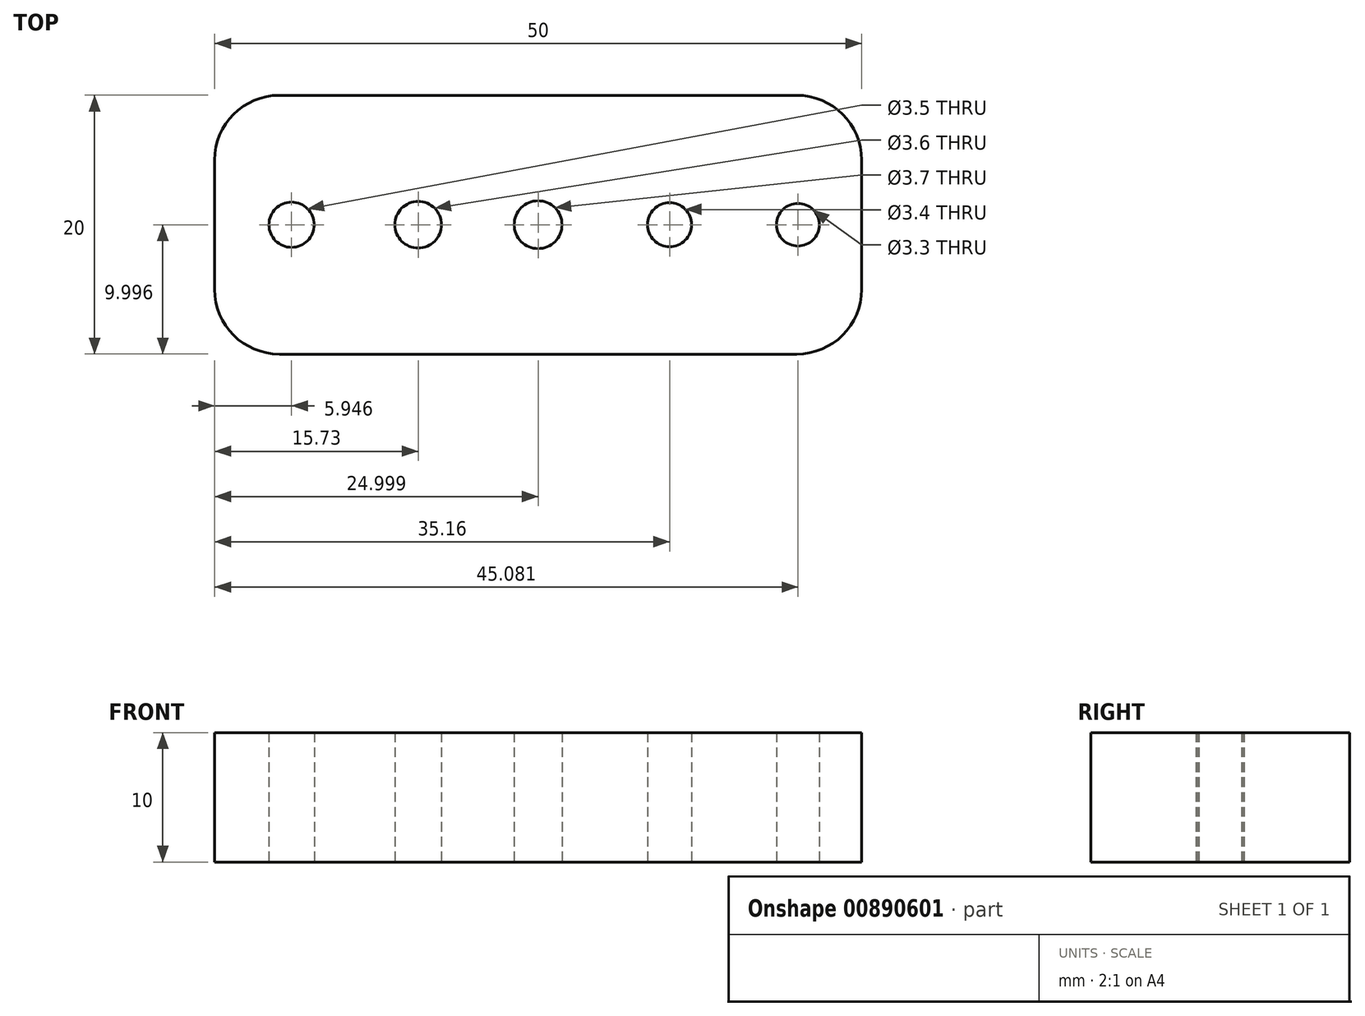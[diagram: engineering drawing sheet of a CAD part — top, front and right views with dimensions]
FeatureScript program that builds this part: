
annotation { "Feature Type Name" : "Feature", "Feature Type Description" : "" }
export const myFeature = defineFeature(function(context is Context, id is Id, definition is map)
    precondition{}
    {
        {
            var Q0;
            Q0=qCreatedBy(makeId("Top.planeOp"),FACE);
            var sketch = newSketch(context, id + "F0", { "sketchPlane" : qUnion([Q0])});
            skLineSegment(sketch, "E0.bottom", {"start": v(-35.16, 0.49) * mm, "end": v(14.84, 0.49) * mm});
            skLineSegment(sketch, "E0.top", {"start": v(-35.16, -19.51) * mm, "end": v(14.84, -19.51) * mm});
            skLineSegment(sketch, "E0.left", {"start": v(-35.16, 0.49) * mm, "end": v(-35.16, -19.51) * mm});
            skLineSegment(sketch, "E0.right", {"start": v(14.84, 0.49) * mm, "end": v(14.84, -19.51) * mm});
            skLineSegment(sketch, "E1", {"start": v(-35.16, -9.51) * mm, "end": v(14.84, -9.51) * mm, "construction": true});
            skCircle(sketch, "E2", {"center": v(-29.21, -9.51) * mm, "radius": 1.75 * mm});
            skCircle(sketch, "E3", {"center": v(-19.43, -9.51) * mm, "radius": 1.8 * mm});
            skCircle(sketch, "E4", {"center": v(-10.16, -9.51) * mm, "radius": 1.85 * mm});
            skCircle(sketch, "E5", {"center": v(0, -9.51) * mm, "radius": 1.7 * mm});
            skCircle(sketch, "E6", {"center": v(9.92, -9.51) * mm, "radius": 1.65 * mm});
            skSolve(sketch);
        }
        {
            var Q0;
            Q0=makeQuery(id+"F0.imprint","IMPRINT",FACE,{"disambiguationData":[TD([[makeQuery(id+"F0.imprint","IMPRINT",EDGE,{"derivedFrom":sQuery(id+"F0.wireOp",EDGE,"E0.bottom")}),-1.0]])]});
            extrude(context, id + "F1", {"entities" : qUnion([Q0]), "depth" : 10 * mm, "offsetDistance" : 25 * mm});
        }
        {
            var Q0;
            Q0=makeQuery(id+"F1.opExtrude","SWEPT_EDGE",EDGE,{"disambiguationData":[OSD([sQuery(id+"F0.wireOp",EDGE,"E0.bottom"),sQuery(id+"F0.wireOp",EDGE,"E0.right")])]});
            var Q1;
            Q1=makeQuery(id+"F1.opExtrude","SWEPT_EDGE",EDGE,{"disambiguationData":[OSD([sQuery(id+"F0.wireOp",EDGE,"E0.top"),sQuery(id+"F0.wireOp",EDGE,"E0.right")])]});
            var Q2;
            Q2=makeQuery(id+"F1.opExtrude","SWEPT_EDGE",EDGE,{"disambiguationData":[OSD([sQuery(id+"F0.wireOp",EDGE,"E0.bottom"),sQuery(id+"F0.wireOp",EDGE,"E0.left")])]});
            var Q3;
            Q3=makeQuery(id+"F1.opExtrude","SWEPT_EDGE",EDGE,{"disambiguationData":[OSD([sQuery(id+"F0.wireOp",EDGE,"E0.top"),sQuery(id+"F0.wireOp",EDGE,"E0.left")])]});
            fillet(context, id + "F2", {"entities" : qUnion([Q0, Q1, Q2, Q3]), "radius" : 5 * mm, "tangentPropagation" : true, "allowEdgeOverflow" : false});
        }
    });
